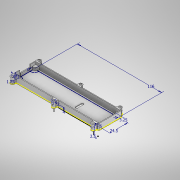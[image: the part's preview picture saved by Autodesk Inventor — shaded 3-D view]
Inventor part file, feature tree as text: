
AUTODESK INVENTOR PART (.ipt)
format: ipt  version: 2021 (Build 250183000, 183)  size: 606,208 bytes
history: native  units: mm
features: extrude x12, sketch x10, projected_geometry x3, fillet x1
ambient origin geometry x8: Origin, YZ Plane, XZ Plane, XY Plane, X Axis, Y Axis, Z Axis, Center Point
bodies: Solid1 (feature_tree)
feature tree (26):
  extrude  "Extrusion1"  Depth=30.0mm
  extrude  "Extrusion2"  Depth=1.0mm
  fillet  "Fillet2"  Radius=1.0mm
  extrude  "Extrusion5"  Depth=17.5mm
  sketch  "Sketch6"  dims[d7=28.0mm d8=1.0mm]
  extrude  "Extrusion6"  Depth=1.0mm
  extrude  "Extrusion7"  Depth=1.0mm
  extrude  "Extrusion8"  Depth=117.5mm
  sketch  "Sketch8"  dims[d11=1.0mm d12=117.5mm]
  extrude  "Extrusion9"  Depth=2.0mm
  extrude  "Extrusion10"  Depth=1.0mm
  extrude  "Extrusion11"  Depth=2.0mm
  extrude  "Extrusion12"  Depth=1.0mm
  sketch  "Sketch11"  dims[d17=2.0mm d18=2.0mm]
  extrude  "Extrusion13"  Depth=2.5mm
  extrude  "Extrusion14"  Depth=2.5mm
  sketch  "Sketch1"  dims[d0=37.0mm d1=30.0mm]
  sketch  "Sketch2"  dims[d2=18.0mm d3=37.5mm d4=1.0mm]
  projected_geometry  "Projected Loop1"
  sketch  "Sketch5"  dims[d5=6.0mm d6=17.5mm]
  projected_geometry  "Projected Loop2"
  sketch  "Sketch7"  dims[d9=1.0mm d10=1.0mm]
  sketch  "Sketch9"  dims[d13=2.0mm d14=2.0mm]
  sketch  "Sketch10"  dims[d15=1.0mm d16=1.0mm]
  projected_geometry  "Projected Loop3"
  sketch  "Sketch12"  dims[d19=2.0mm d20=2.0mm d21=2.5mm d22=2.5mm d23=5.0mm d24=2.5mm d25=2.5mm d26=2.5mm d27=2.5mm d28=5.0mm d29=5.0mm d30=2.5mm d31=3.1mm d32=3.1mm d33=3.1mm d34=3.1mm d35=3.1mm d36=3.1mm d37=7.0mm d38=0.0mm d39=1.0mm d40=0.0mm d44=1.0mm d45=1.0mm d46=0.5mm d47=0.0mm d48=1.0mm d49=1.0mm d50=1.0mm d51=1.0mm d53=1.0mm d61=7.0mm d62=0.0mm d63=24.5mm d64=116.0mm d65=1.25mm d66=3.25mm d67=6.0mm d68=6.0mm d69=4.0mm d70=0.0mm d71=5.0mm d72=5.0mm d73=3.5mm d74=0.0mm d75=3.0mm d76=3.0mm d77=3.13mm d78=5.1mm d79=5.1mm d80=0.0mm d81=42.13mm d82=0.0mm d83=0.0mm d84=2.0mm d85=2.0mm d87=2.5mm d88=2.5mm d89=4.0mm d90=10.0mm d91=0.0mm d92=2.0mm d93=2.5mm d94=20.0mm d95=0.0mm d96=30.0mm d97=1.0mm d98=20.0mm d99=0.0mm d100=116.5mm d101=1.0mm d102=5.0mm d103=5.0mm d104=5.0mm d105=5.0mm d106=20.0mm d107=0.0mm d108=20.0mm d109=0.0mm d110=1.0mm d111=1.0mm d112=20.0mm d113=0.0mm]
